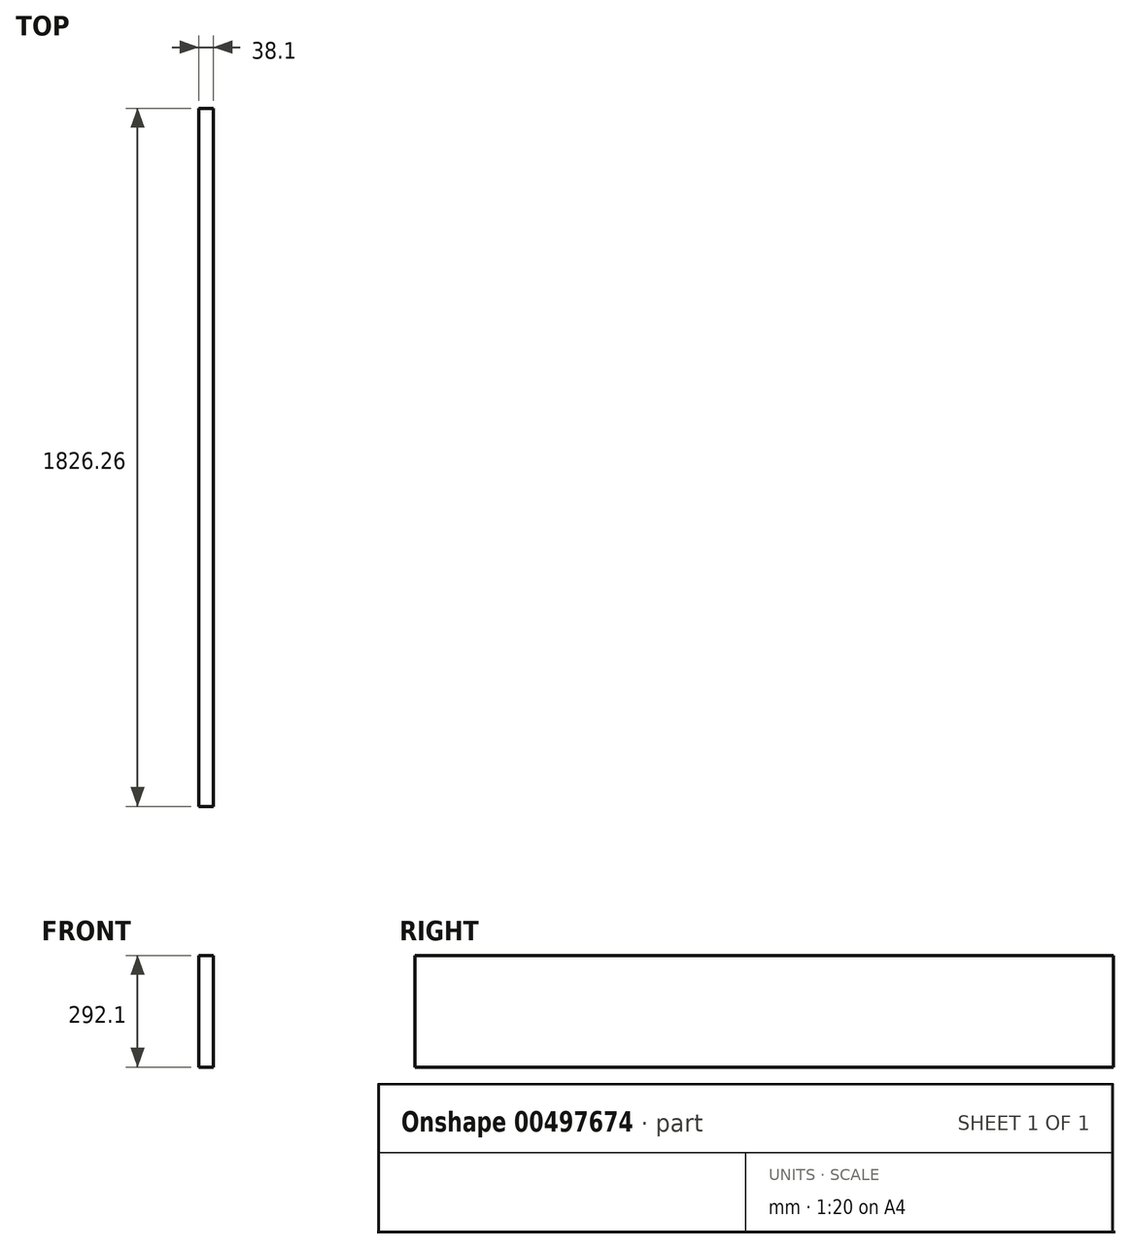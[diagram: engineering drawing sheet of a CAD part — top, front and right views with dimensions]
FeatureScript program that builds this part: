
annotation { "Feature Type Name" : "Feature", "Feature Type Description" : "" }
export const myFeature = defineFeature(function(context is Context, id is Id, definition is map)
    precondition{}
    {
        {
            var Q0;
            Q0=qCreatedBy(makeId("Front.planeOp"),FACE);
            var sketch = newSketch(context, id + "F0", { "sketchPlane" : qUnion([Q0])});
            skLineSegment(sketch, "E0.bottom", {"start": v(0, 0) * mm, "end": v(38.1, 0) * mm});
            skLineSegment(sketch, "E0.top", {"start": v(0, 292.1) * mm, "end": v(38.1, 292.1) * mm});
            skLineSegment(sketch, "E0.left", {"start": v(0, 0) * mm, "end": v(0, 292.1) * mm});
            skLineSegment(sketch, "E0.right", {"start": v(38.1, 0) * mm, "end": v(38.1, 292.1) * mm});
            skSolve(sketch);
        }
        {
            var Q0;
            Q0 = qSketchRegion(id + "F0", true);
            extrude(context, id + "F1", {"entities" : qUnion([Q0]), "depth" : 1826.26 * mm});
        }
    });
